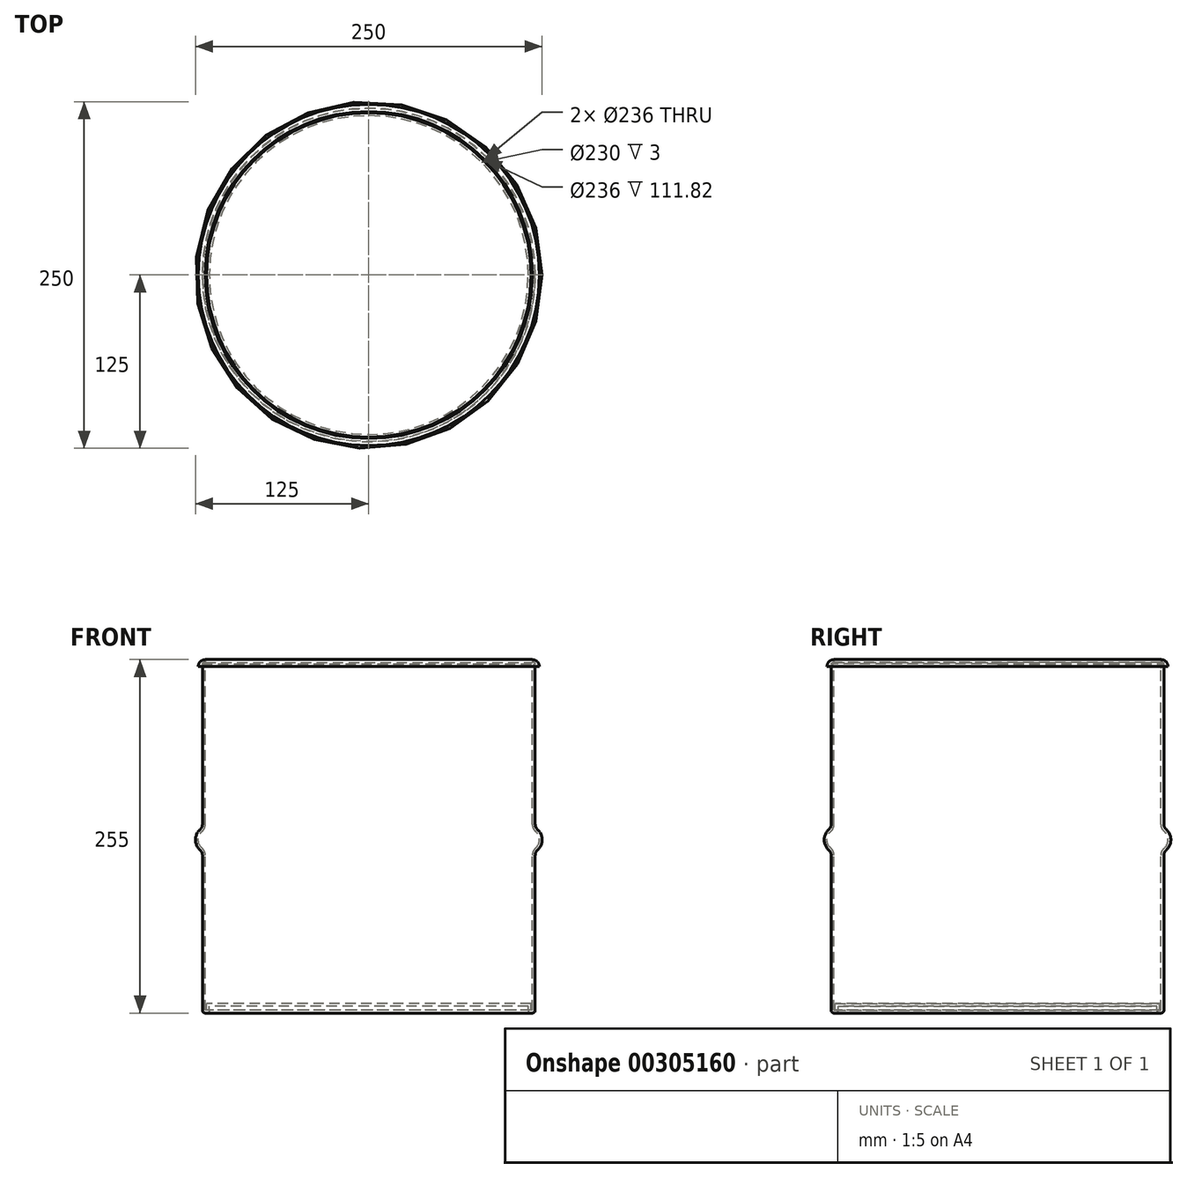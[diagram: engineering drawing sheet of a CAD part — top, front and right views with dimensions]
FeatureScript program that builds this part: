
annotation { "Feature Type Name" : "Feature", "Feature Type Description" : "" }
export const myFeature = defineFeature(function(context is Context, id is Id, definition is map)
    precondition{}
    {
        {
            var Q0;
            Q0=qCreatedBy(makeId("Front.planeOp"),FACE);
            var sketch = newSketch(context, id + "F0", { "sketchPlane" : qUnion([Q0])});
            skLineSegment(sketch, "E0", {"start": v(0, 0) * mm, "end": v(-115, 0) * mm});
            skLineSegment(sketch, "E1", {"start": v(-115, 0) * mm, "end": v(-115, -5) * mm});
            skLineSegment(sketch, "E2", {"start": v(-115, -5) * mm, "end": v(-120, -5) * mm});
            skLineSegment(sketch, "E3", {"start": v(-120, -5) * mm, "end": v(-120, 111.34) * mm});
            skLineSegment(sketch, "E4", {"start": v(-120, 128.66) * mm, "end": v(-120, 245) * mm});
            skLineSegment(sketch, "E5", {"start": v(-120, 245) * mm, "end": v(-123, 245) * mm});
            skLineSegment(sketch, "E6", {"start": v(-123, 245) * mm, "end": v(-123, 250) * mm});
            skLineSegment(sketch, "E7", {"start": v(-123, 250) * mm, "end": v(0, 250) * mm});
            skLineSegment(sketch, "E8", {"start": v(0, 250) * mm, "end": v(0, 0) * mm});
            skArc(sketch, "E9", {"start": v(-120, 128.66) * mm, "mid": v(-125, 120) * mm, "end": v(-120, 111.34) * mm});
            skSolve(sketch);
        }
        {
            var Q0;
            Q0=qSketchRegion(id+"F0",true);
            var Q1;
            Q1=sQuery(id+"F0.wireOp",EDGE,"E8");
            revolve(context, id + "F1", {"surfaceOperationType" : NewSurfaceOperationType.NEW, "entities" : qUnion([Q0]), "axis" : qUnion([Q1]), "revolveType" : RevolveType.FULL});
        }
        {
            var Q0;
            Q0=makeQuery(id+"F1.opRevolve","SWEPT_EDGE",EDGE,{"disambiguationData":[OSD([sQuery(id+"F0.wireOp",EDGE,"E4"),sQuery(id+"F0.wireOp",EDGE,"E9")])]});
            var Q1;
            Q1=makeQuery(id+"F1.opRevolve","SWEPT_EDGE",EDGE,{"disambiguationData":[OSD([sQuery(id+"F0.wireOp",EDGE,"E3"),sQuery(id+"F0.wireOp",EDGE,"E9")])]});
            fillet(context, id + "F2", {"entities" : qUnion([Q0, Q1]), "radius" : 5 * mm, "tangentPropagation" : true, "allowEdgeOverflow" : false});
        }
        {
            var Q0;
            Q0=makeQuery(id+"F1.opRevolve","SWEPT_EDGE",EDGE,{"disambiguationData":[OSD([sQuery(id+"F0.wireOp",EDGE,"E6"),sQuery(id+"F0.wireOp",EDGE,"E7")])]});
            fillet(context, id + "F3", {"entities" : qUnion([Q0]), "radius" : 5 * mm, "tangentPropagation" : true, "allowEdgeOverflow" : false});
        }
        {
            var Q0;
            Q0=makeQuery(id+"F1.opRevolve","SWEPT_EDGE",EDGE,{"disambiguationData":[OSD([sQuery(id+"F0.wireOp",EDGE,"E4"),sQuery(id+"F0.wireOp",EDGE,"E5")])]});
            fillet(context, id + "F4", {"entities" : qUnion([Q0]), "radius" : 1 * mm, "tangentPropagation" : true, "allowEdgeOverflow" : false});
        }
        {
            var Q0;
            Q0=makeQuery(id+"F1.opRevolve","SWEPT_EDGE",EDGE,{"disambiguationData":[OSD([sQuery(id+"F0.wireOp",EDGE,"E2"),sQuery(id+"F0.wireOp",EDGE,"E3")])]});
            var Q1;
            Q1=makeQuery(id+"F1.opRevolve","SWEPT_EDGE",EDGE,{"disambiguationData":[OSD([sQuery(id+"F0.wireOp",EDGE,"E1"),sQuery(id+"F0.wireOp",EDGE,"E2")])]});
            fillet(context, id + "F5", {"entities" : qUnion([Q0, Q1]), "radius" : 2 * mm, "tangentPropagation" : true, "allowEdgeOverflow" : false});
        }
        {
            var Q0;
            Q0=makeQuery(id+"F1.opRevolve","SWEPT_FACE",FACE,{"disambiguationData":[OSD([sQuery(id+"F0.wireOp",EDGE,"E7")])]});
            shell(context, id + "F6", {"entities" : qUnion([Q0]), "thickness" : 2 * mm});
        }
    });
